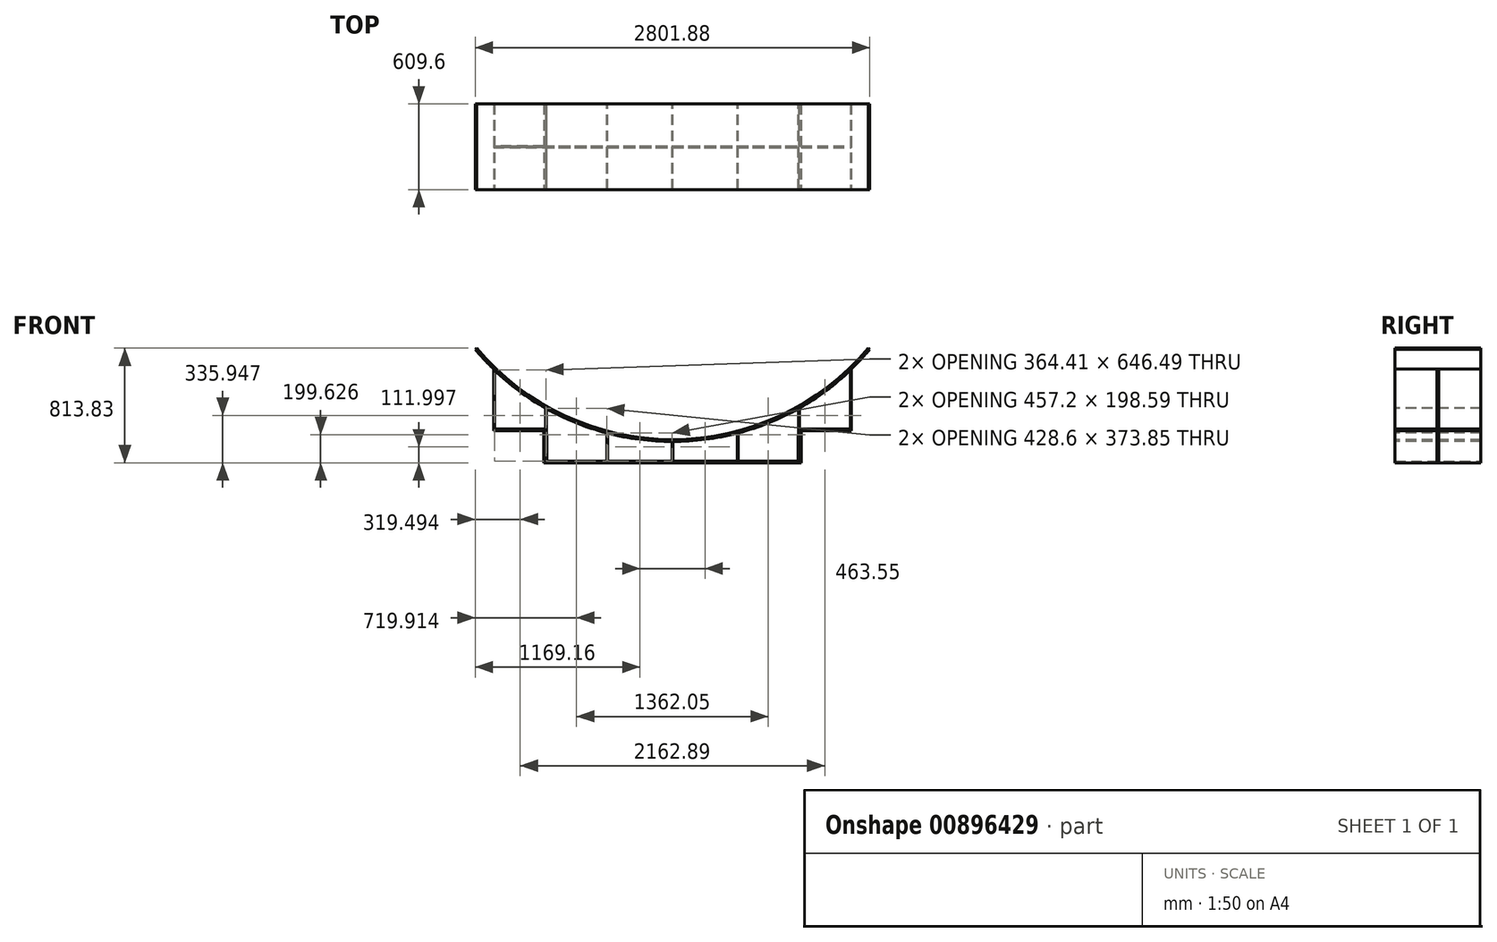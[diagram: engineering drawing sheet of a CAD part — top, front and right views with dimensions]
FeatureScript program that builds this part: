
annotation { "Feature Type Name" : "Feature", "Feature Type Description" : "" }
export const myFeature = defineFeature(function(context is Context, id is Id, definition is map)
    precondition{}
    {
        {
            var Q0;
            Q0=qCreatedBy(makeId("Front.planeOp"),FACE);
            var sketch = newSketch(context, id + "F0", { "sketchPlane" : qUnion([Q0])});
            skLineSegment(sketch, "E0.bottom", {"start": v(0, 0) * mm, "end": v(-914.4, 0) * mm});
            skLineSegment(sketch, "E0.top", {"start": v(0, 12.7) * mm, "end": v(-901.7, 12.7) * mm});
            skLineSegment(sketch, "E0.left", {"start": v(0, 0) * mm, "end": v(0, 12.7) * mm});
            skLineSegment(sketch, "E0.right", {"start": v(-914.4, 0) * mm, "end": v(-914.4, 12.7) * mm});
            skLineSegment(sketch, "E1.top", {"start": v(-914.4, 241.3) * mm, "end": v(-901.7, 241.3) * mm});
            skLineSegment(sketch, "E1.left", {"start": v(-914.4, 12.7) * mm, "end": v(-914.4, 228.6) * mm});
            skLineSegment(sketch, "E1.right", {"start": v(-901.7, 12.7) * mm, "end": v(-901.7, 241.3) * mm});
            skLineSegment(sketch, "E2.bottom", {"start": v(-914.4, 241.3) * mm, "end": v(-1270, 241.3) * mm});
            skLineSegment(sketch, "E2.top", {"start": v(-914.4, 228.6) * mm, "end": v(-1270, 228.6) * mm});
            skLineSegment(sketch, "E2.right", {"start": v(-1270, 241.3) * mm, "end": v(-1270, 228.6) * mm});
            skSolve(sketch);
        }
        {
            var Q0;
            Q0 = qSketchRegion(id + "F0", true);
            extrude(context, id + "F1", {"entities" : qUnion([Q0]), "oppositeDirection" : true, "depth" : 609.6 * mm, "offsetDistance" : 25.4 * mm});
        }
        {
            var Q0;
            Q0=makeQuery(id+"F1.opExtrude","SWEPT_BODY",BODY,{"disambiguationData":[OSD([sQuery(id+"F0.wireOp",EDGE,"E0.bottom"),sQuery(id+"F0.wireOp",EDGE,"E0.top"),sQuery(id+"F0.wireOp",EDGE,"E0.left"),sQuery(id+"F0.wireOp",EDGE,"E0.right"),sQuery(id+"F0.wireOp",EDGE,"E1.top"),sQuery(id+"F0.wireOp",EDGE,"E1.left"),sQuery(id+"F0.wireOp",EDGE,"E1.right"),sQuery(id+"F0.wireOp",EDGE,"E2.bottom"),sQuery(id+"F0.wireOp",EDGE,"E2.top"),sQuery(id+"F0.wireOp",EDGE,"E2.right")])]});
            var Q1;
            Q1=qCreatedBy(makeId("Right.planeOp"),FACE);
            mirror(context, id + "F2", {"operationType" : NewBodyOperationType.ADD, "entities" : qUnion([Q0]), "mirrorPlane" : qUnion([Q1])});
        }
        {
            var Q0;
            Q0=qCreatedBy(makeId("Front.planeOp"),FACE);
            var sketch = newSketch(context, id + "F3", { "sketchPlane" : qUnion([Q0])});
            skArc(sketch, "E3", {"start": v(-1400.94, 805.67) * mm, "mid": v(0, 152.4) * mm, "end": v(1400.94, 805.67) * mm});
            skArc(sketch, "E4", {"start": v(-1391.21, 813.83) * mm, "mid": v(0, 165.1) * mm, "end": v(1391.21, 813.83) * mm});
            skLineSegment(sketch, "E5", {"start": v(0, 1981.2) * mm, "end": v(-1400.94, 805.67) * mm});
            skLineSegment(sketch, "E6", {"start": v(0, 1981.2) * mm, "end": v(1400.94, 805.67) * mm});
            skLineSegment(sketch, "E7", {"start": v(0, 1981.2) * mm, "end": v(0, 165.1) * mm});
            skSolve(sketch);
        }
        {
            var Q0;
            {var subQ1=sQuery(id+"F3.wireOp",EDGE,"E3");Q0=makeQuery(id+"F3.imprint","IMPRINT",FACE,{"disambiguationData":[TD([[makeQuery(id+"F3.imprint","IMPRINT",EDGE,{"derivedFrom":subQ1}),1.0]])]});}
            extrude(context, id + "F4", {"entities" : qUnion([Q0]), "oppositeDirection" : true, "depth" : 609.6 * mm, "offsetDistance" : 25.4 * mm});
        }
        {
            var Q0;
            Q0=qCreatedBy(makeId("Front.planeOp"),FACE);
            var sketch = newSketch(context, id + "F5", { "sketchPlane" : qUnion([Q0])});
            skLineSegment(sketch, "E8.bottom", {"start": v(0, 0) * mm, "end": v(-3.18, 0) * mm});
            skLineSegment(sketch, "E8.top", {"start": v(0, 254) * mm, "end": v(-3.18, 254) * mm});
            skLineSegment(sketch, "E8.left", {"start": v(0, 0) * mm, "end": v(0, 152.4) * mm});
            skLineSegment(sketch, "E8.right", {"start": v(-3.18, 0) * mm, "end": v(-3.18, 152.4) * mm});
            skCircle(sketch, "E9", {"center": v(0, 1981.2) * mm, "radius": 1828.8 * mm});
            skLineSegment(sketch, "E10.bottom", {"start": v(-460.38, 0) * mm, "end": v(-466.73, 0) * mm});
            skLineSegment(sketch, "E10.left", {"start": v(-460.38, 0) * mm, "end": v(-460.38, 211.3) * mm});
            skLineSegment(sketch, "E10.right", {"start": v(-466.73, 0) * mm, "end": v(-466.73, 212.96) * mm});
            skLineSegment(sketch, "E11.bottom", {"start": v(-899.16, 0) * mm, "end": v(-892.81, 0) * mm});
            skLineSegment(sketch, "E11.left", {"start": v(-892.81, 0) * mm, "end": v(-895.33, 386.55) * mm});
            skLineSegment(sketch, "E11.right", {"start": v(-899.16, 0) * mm, "end": v(-901.7, 390.15) * mm});
            skLineSegment(sketch, "E12.bottom", {"start": v(-1270, 241.3) * mm, "end": v(-1263.65, 241.3) * mm});
            skLineSegment(sketch, "E12.left", {"start": v(-1270, 241.3) * mm, "end": v(-1270, 665.3) * mm});
            skLineSegment(sketch, "E12.right", {"start": v(-1263.65, 241.3) * mm, "end": v(-1263.65, 659.2) * mm});
            skSolve(sketch);
        }
        {
            var Q0;
            Q0=makeQuery(id+"F5.imprint","IMPRINT",FACE,{"disambiguationData":[TD([[makeQuery(id+"F5.imprint","IMPRINT",EDGE,{"derivedFrom":sQuery(id+"F5.wireOp",EDGE,"E12.bottom")}),1.0]])]});
            var Q1;
            Q1=makeQuery(id+"F5.imprint","IMPRINT",FACE,{"disambiguationData":[TD([[makeQuery(id+"F5.imprint","IMPRINT",EDGE,{"derivedFrom":sQuery(id+"F5.wireOp",EDGE,"E10.bottom")}),-1.0]])]});
            var Q2;
            Q2=makeQuery(id+"F5.imprint","IMPRINT",FACE,{"disambiguationData":[TD([[makeQuery(id+"F5.imprint","IMPRINT",EDGE,{"derivedFrom":sQuery(id+"F5.wireOp",EDGE,"E8.bottom")}),-1.0]])]});
            var Q3;
            Q3=makeQuery(id+"F5.imprint","IMPRINT",FACE,{"disambiguationData":[TD([[makeQuery(id+"F5.imprint","IMPRINT",EDGE,{"derivedFrom":sQuery(id+"F5.wireOp",EDGE,"E11.bottom")}),1.0]])]});
            extrude(context, id + "F6", {"entities" : qUnion([Q0, Q1, Q2, Q3]), "operationType" : NewBodyOperationType.ADD, "oppositeDirection" : true, "depth" : 609.6 * mm, "offsetDistance" : 25.4 * mm});
        }
        {
            var Q0;
            Q0=makeQuery(id+"F1.opExtrude","SWEPT_BODY",BODY,{"disambiguationData":[OSD([sQuery(id+"F0.wireOp",EDGE,"E0.bottom"),sQuery(id+"F0.wireOp",EDGE,"E0.top"),sQuery(id+"F0.wireOp",EDGE,"E0.left"),sQuery(id+"F0.wireOp",EDGE,"E0.right"),sQuery(id+"F0.wireOp",EDGE,"E1.top"),sQuery(id+"F0.wireOp",EDGE,"E1.left"),sQuery(id+"F0.wireOp",EDGE,"E1.right"),sQuery(id+"F0.wireOp",EDGE,"E2.bottom"),sQuery(id+"F0.wireOp",EDGE,"E2.top"),sQuery(id+"F0.wireOp",EDGE,"E2.right")])]});
            var Q1;
            Q1=qCreatedBy(makeId("Right.planeOp"),FACE);
            mirror(context, id + "F7", {"entities" : qUnion([Q0]), "mirrorPlane" : qUnion([Q1])});
        }
        {
            var Q0;
            Q0=qCreatedBy(makeId("Front.planeOp"),FACE);
            var sketch = newSketch(context, id + "F8", { "sketchPlane" : qUnion([Q0])});
            skLineSegment(sketch, "E13.top", {"start": v(-914.4, 0) * mm, "end": v(914.4, 0) * mm});
            skLineSegment(sketch, "E13.left", {"start": v(-1270, 665.3) * mm, "end": v(-1270, 228.6) * mm});
            skLineSegment(sketch, "E13.right", {"start": v(1270, 665.3) * mm, "end": v(1270, 228.6) * mm});
            skLineSegment(sketch, "E14", {"start": v(-1270, 228.6) * mm, "end": v(-914.4, 228.6) * mm});
            skLineSegment(sketch, "E15", {"start": v(-914.4, 228.6) * mm, "end": v(-914.4, 0) * mm});
            skLineSegment(sketch, "E16", {"start": v(1270, 228.6) * mm, "end": v(914.4, 228.6) * mm});
            skLineSegment(sketch, "E17", {"start": v(914.4, 228.6) * mm, "end": v(914.4, 0) * mm});
            skArc(sketch, "E18", {"start": v(-1270, 663.53) * mm, "mid": v(0, 151.13) * mm, "end": v(1270, 663.53) * mm});
            skSolve(sketch);
        }
        {
            var Q0;
            Q0=qCreatedBy(makeId("Front.planeOp"),FACE);
            cPlane(context, id + "F9", {"entities" : qUnion([Q0]), "cplaneType" : CPlaneType.OFFSET, "offset" : 298.45 * mm, "oppositeDirection" : true, "width" : 152.4 * mm, "height" : 152.4 * mm});
        }
        {
            var Q0;
            Q0=qCreatedBy(id+"F9.planeOp",FACE);
            var sketch = newSketch(context, id + "F10", { "sketchPlane" : qUnion([Q0])});
            skLineSegment(sketch, "E19.top", {"start": v(-914.4, 0) * mm, "end": v(914.4, 0) * mm});
            skLineSegment(sketch, "E19.left", {"start": v(-1270, 665.3) * mm, "end": v(-1270, 228.6) * mm});
            skLineSegment(sketch, "E19.right", {"start": v(1270, 665.3) * mm, "end": v(1270, 228.6) * mm});
            skLineSegment(sketch, "E20", {"start": v(-914.4, 0) * mm, "end": v(-914.4, 228.6) * mm});
            skLineSegment(sketch, "E21", {"start": v(-914.4, 228.6) * mm, "end": v(-1270, 228.6) * mm});
            skLineSegment(sketch, "E22", {"start": v(914.4, 0) * mm, "end": v(914.4, 228.6) * mm});
            skLineSegment(sketch, "E23", {"start": v(914.4, 228.6) * mm, "end": v(1270, 228.6) * mm});
            skArc(sketch, "E24", {"start": v(-1270, 663.53) * mm, "mid": v(0, 151.13) * mm, "end": v(1270, 663.53) * mm});
            skSolve(sketch);
        }
        {
            var Q0;
            Q0=makeQuery(id+"F10.imprint","IMPRINT",FACE,{"disambiguationData":[TD([[makeQuery(id+"F10.imprint","IMPRINT",EDGE,{"derivedFrom":sQuery(id+"F10.wireOp",EDGE,"E19.top")}),1.0]])]});
            extrude(context, id + "F11", {"entities" : qUnion([Q0]), "oppositeDirection" : true, "depth" : 12.7 * mm, "offsetDistance" : 25.4 * mm});
        }
    });
